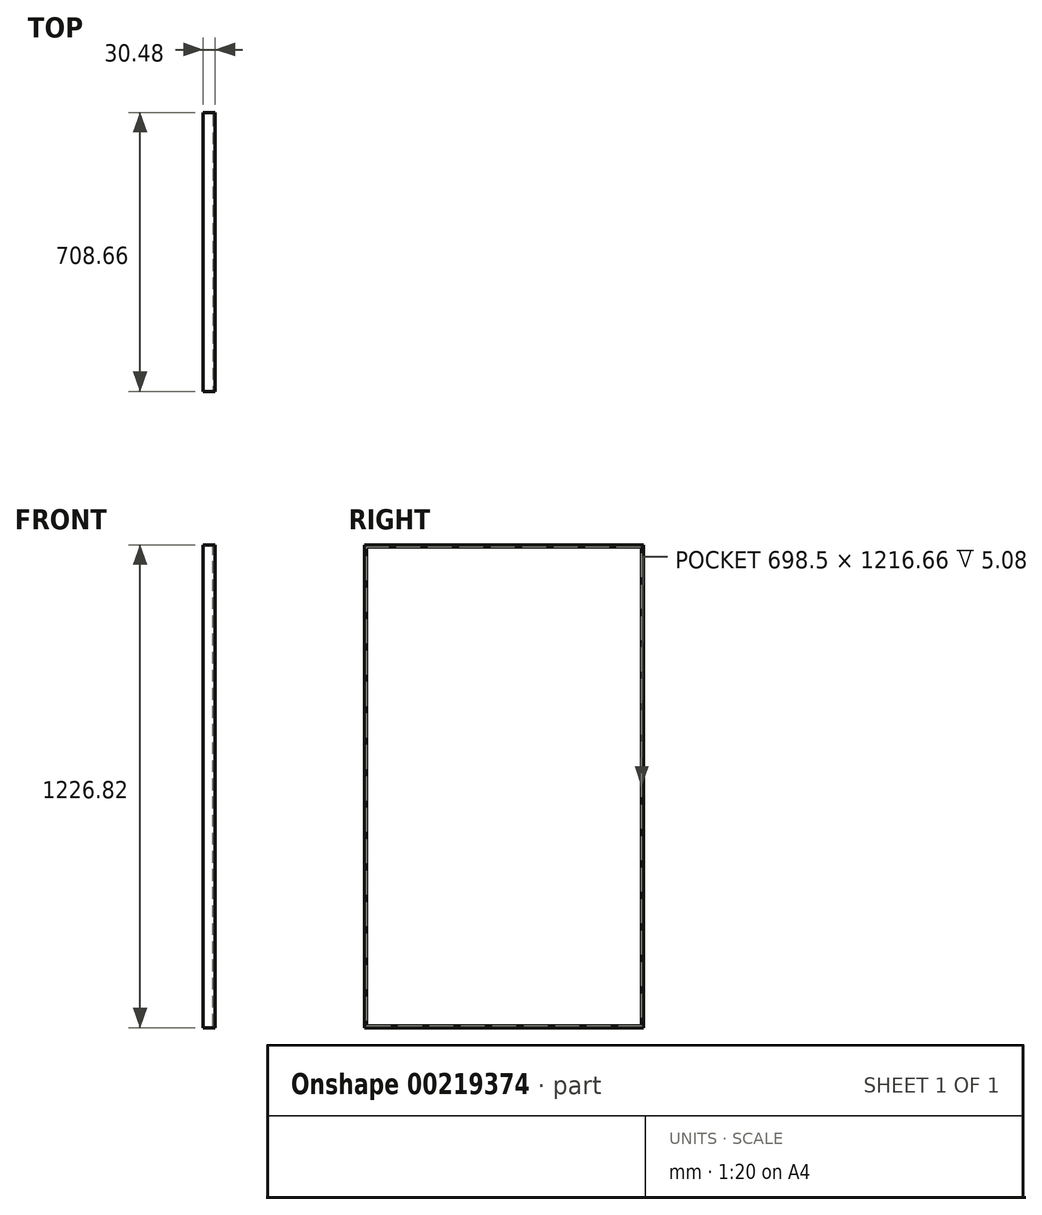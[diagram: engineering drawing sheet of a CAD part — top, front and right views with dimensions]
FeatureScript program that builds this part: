
annotation { "Feature Type Name" : "Feature", "Feature Type Description" : "" }
export const myFeature = defineFeature(function(context is Context, id is Id, definition is map)
    precondition{}
    {
        {
            var Q0;
            Q0=qCreatedBy(makeId("Right.planeOp"),FACE);
            var sketch = newSketch(context, id + "F0", { "sketchPlane" : qUnion([Q0])});
            skLineSegment(sketch, "E0.bottom", {"start": v(354.33, -613.4) * mm, "end": v(-354.33, -613.4) * mm});
            skLineSegment(sketch, "E0.top", {"start": v(354.33, 613.41) * mm, "end": v(-354.33, 613.41) * mm});
            skLineSegment(sketch, "E0.left", {"start": v(354.33, -613.4) * mm, "end": v(354.33, 613.41) * mm});
            skLineSegment(sketch, "E0.right", {"start": v(-354.33, -613.41) * mm, "end": v(-354.33, 613.4) * mm});
            skPoint(sketch, "E0.middle", {"position": v(0, 0) * mm});
            skLineSegment(sketch, "E1.bottom", {"start": v(349.25, -608.33) * mm, "end": v(-349.25, -608.33) * mm});
            skLineSegment(sketch, "E1.top", {"start": v(349.25, 608.33) * mm, "end": v(-349.25, 608.33) * mm});
            skLineSegment(sketch, "E1.left", {"start": v(349.25, -608.33) * mm, "end": v(349.25, 608.33) * mm});
            skLineSegment(sketch, "E1.right", {"start": v(-349.25, -608.33) * mm, "end": v(-349.25, 608.33) * mm});
            skSolve(sketch);
        }
        {
            var Q0;
            Q0=makeQuery(id+"F0.imprint","IMPRINT",FACE,{"disambiguationData":[TD([[makeQuery(id+"F0.imprint","IMPRINT",EDGE,{"derivedFrom":sQuery(id+"F0.wireOp",EDGE,"E1.bottom")}),-1.0]])]});
            extrude(context, id + "F1", {"entities" : qUnion([Q0]), "depth" : 25.4 * mm});
        }
        {
            var Q0;
            Q0=makeQuery(id+"F0.imprint","IMPRINT",FACE,{"disambiguationData":[TD([[makeQuery(id+"F0.imprint","IMPRINT",EDGE,{"derivedFrom":sQuery(id+"F0.wireOp",EDGE,"E0.bottom")}),-1.0]])]});
            extrude(context, id + "F2", {"entities" : qUnion([Q0]), "operationType" : NewBodyOperationType.ADD, "depth" : 30.48 * mm});
        }
    });
